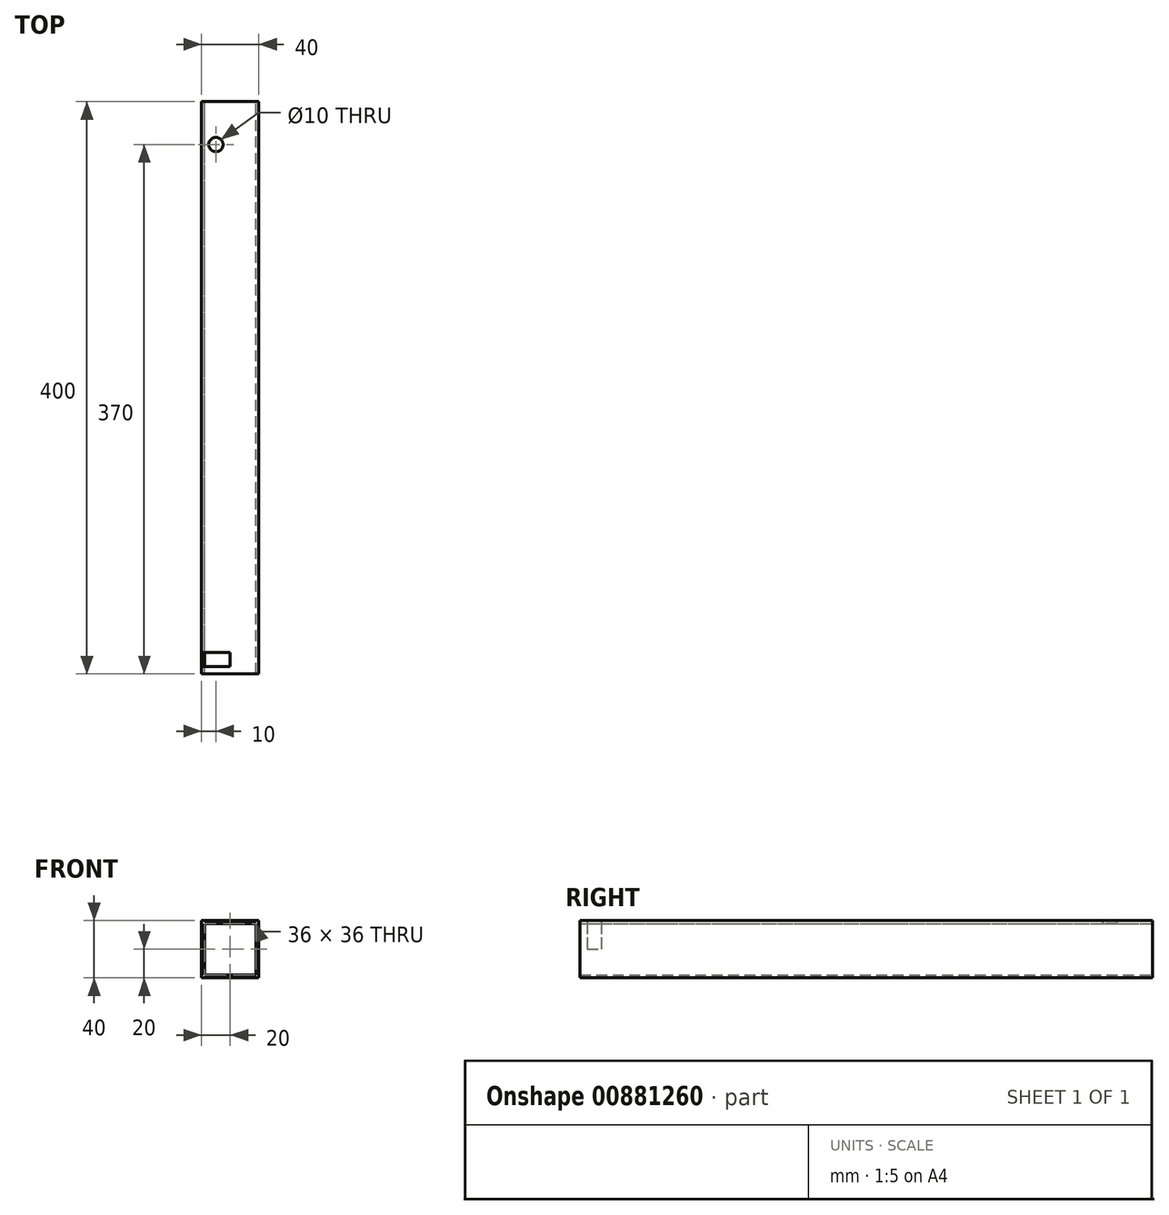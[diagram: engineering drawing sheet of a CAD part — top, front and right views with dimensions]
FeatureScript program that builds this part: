
annotation { "Feature Type Name" : "Feature", "Feature Type Description" : "" }
export const myFeature = defineFeature(function(context is Context, id is Id, definition is map)
    precondition{}
    {
        {
            var Q0;
            Q0=qCreatedBy(makeId("Front.planeOp"),FACE);
            var sketch = newSketch(context, id + "F0", { "sketchPlane" : qUnion([Q0])});
            skLineSegment(sketch, "E0.bottom", {"start": v(-20, 20) * mm, "end": v(20, 20) * mm});
            skLineSegment(sketch, "E0.top", {"start": v(-20, -20) * mm, "end": v(20, -20) * mm});
            skLineSegment(sketch, "E0.left", {"start": v(-20, 20) * mm, "end": v(-20, -20) * mm});
            skLineSegment(sketch, "E0.right", {"start": v(20, 20) * mm, "end": v(20, -20) * mm});
            skLineSegment(sketch, "E1.bottom", {"start": v(-18, 18) * mm, "end": v(18, 18) * mm});
            skLineSegment(sketch, "E1.top", {"start": v(-18, -18) * mm, "end": v(18, -18) * mm});
            skLineSegment(sketch, "E1.left", {"start": v(-18, 18) * mm, "end": v(-18, -18) * mm});
            skLineSegment(sketch, "E1.right", {"start": v(18, 18) * mm, "end": v(18, -18) * mm});
            skLineSegment(sketch, "E2", {"start": v(-20, 20) * mm, "end": v(20, -20) * mm, "construction": true});
            skLineSegment(sketch, "E3", {"start": v(20, 20) * mm, "end": v(-20, -20) * mm, "construction": true});
            skSolve(sketch);
        }
        {
            var Q0;
            Q0=makeQuery(id+"F0.imprint","IMPRINT",FACE,{"disambiguationData":[TD([[makeQuery(id+"F0.imprint","IMPRINT",EDGE,{"derivedFrom":sQuery(id+"F0.wireOp",EDGE,"E0.bottom")}),-1.0]])]});
            extrude(context, id + "F1", {"entities" : qUnion([Q0]), "endBound" : BoundingType.SYMMETRIC, "depth" : 400 * mm, "offsetDistance" : 25 * mm});
        }
        {
            var Q0;
            Q0=qCreatedBy(makeId("Right.planeOp"),FACE);
            var sketch = newSketch(context, id + "F2", { "sketchPlane" : qUnion([Q0])});
            skLineSegment(sketch, "E4.bottom", {"start": v(-195, 30) * mm, "end": v(-185, 30) * mm});
            skLineSegment(sketch, "E4.top", {"start": v(-195, 0) * mm, "end": v(-185, 0) * mm});
            skLineSegment(sketch, "E4.left", {"start": v(-195, 30) * mm, "end": v(-195, 0) * mm});
            skLineSegment(sketch, "E4.right", {"start": v(-185, 30) * mm, "end": v(-185, 0) * mm});
            skSolve(sketch);
        }
        {
            var Q0;
            Q0=makeQuery(id+"F2.imprint","IMPRINT",FACE,{"disambiguationData":[TD([[makeQuery(id+"F2.imprint","IMPRINT",EDGE,{"derivedFrom":sQuery(id+"F2.wireOp",EDGE,"E4.bottom")}),-1.0]])]});
            extrude(context, id + "F3", {"entities" : qUnion([Q0]), "operationType" : NewBodyOperationType.REMOVE, "endBound" : BoundingType.THROUGH_ALL, "oppositeDirection" : true, "depth" : 25 * mm, "offsetDistance" : 25 * mm});
        }
        {
            var Q0;
            Q0=qCreatedBy(makeId("Top.planeOp"),FACE);
            var sketch = newSketch(context, id + "F4", { "sketchPlane" : qUnion([Q0])});
            skCircle(sketch, "E5", {"center": v(-10, 170) * mm, "radius": 5 * mm});
            skSolve(sketch);
        }
        {
            var Q0;
            Q0 = qSketchRegion(id + "F4", true);
            extrude(context, id + "F5", {"entities" : qUnion([Q0]), "operationType" : NewBodyOperationType.REMOVE, "endBound" : BoundingType.THROUGH_ALL, "depth" : 25 * mm, "offsetDistance" : 25 * mm});
        }
    });
